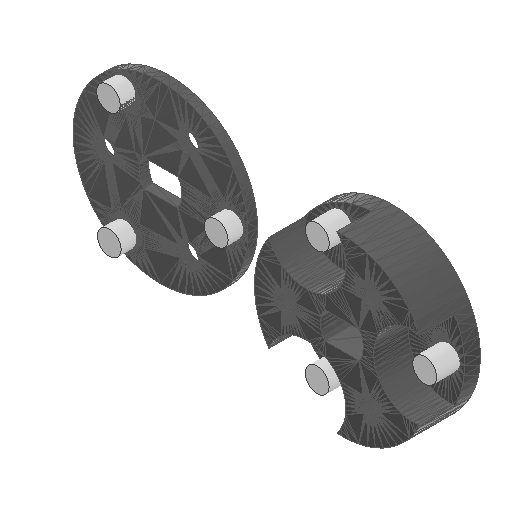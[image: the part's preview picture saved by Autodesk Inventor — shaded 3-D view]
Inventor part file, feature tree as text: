
AUTODESK INVENTOR PART (.ipt)
format: ipt  version: 2022 (Build 260153000, 153)  size: 223,744 bytes
history: native  units: mm
features: extrude x2, sketch x2, other x1
ambient origin geometry x8: Origin, YZ Plane, XZ Plane, XY Plane, X Axis, Y Axis, Z Axis, Center Point
bodies: Volumenkörper1 (feature_tree)
feature tree (5):
  extrude  "Extrusion1"  Depth=3.0mm
  extrude  "Extrusion2"  Depth=3.0mm TaperAngle=0.0deg
  sketch  "Skizze1"  dims[d0=3.0mm d1=3.0mm]
  sketch  "Skizze2"  dims[d2=3.0mm d3=3.0mm d4=0.0mm d5=3.0mm d6=3.0mm d7=3.0mm d8=2.0mm d9=0.0mm]
  other  "MeshFeature1"
